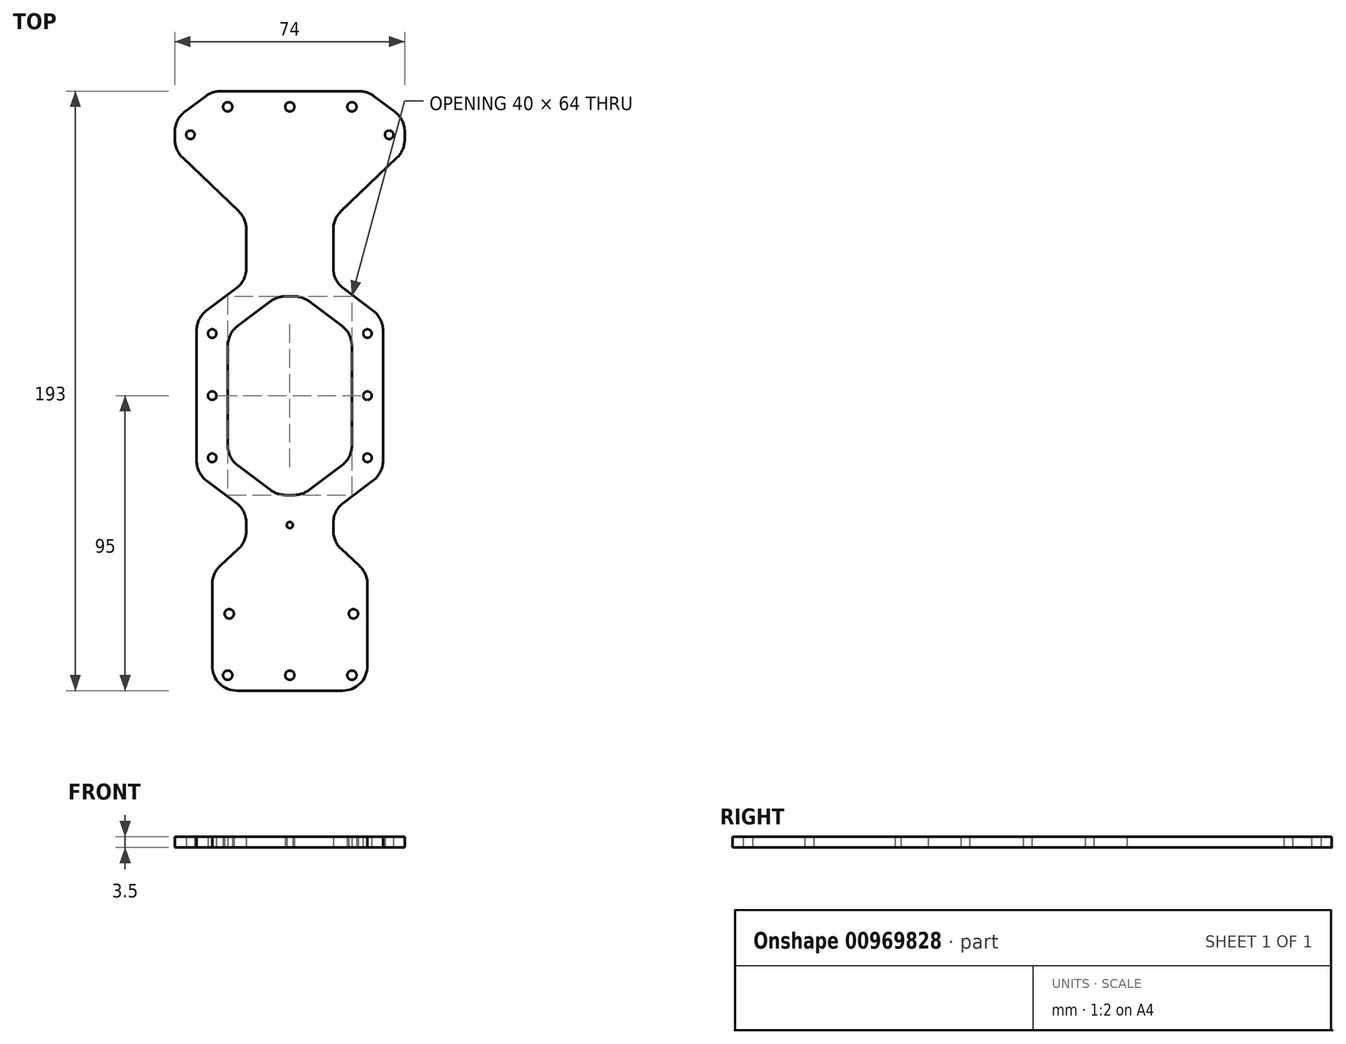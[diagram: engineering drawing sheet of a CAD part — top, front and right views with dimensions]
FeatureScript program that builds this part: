
annotation { "Feature Type Name" : "Feature", "Feature Type Description" : "" }
export const myFeature = defineFeature(function(context is Context, id is Id, definition is map)
    precondition{}
    {
        {
            var Q0;
            Q0=qCreatedBy(makeId("Top.planeOp"),FACE);
            var sketch = newSketch(context, id + "F0", { "sketchPlane" : qUnion([Q0])});
            skCircle(sketch, "E0", {"center": v(-32, 86) * mm, "radius": 1.38 * mm});
            skCircle(sketch, "E1", {"center": v(0, 95) * mm, "radius": 1.5 * mm});
            skCircle(sketch, "E2", {"center": v(-20, 95) * mm, "radius": 1.5 * mm});
            skCircle(sketch, "E3", {"center": v(32, 86) * mm, "radius": 1.38 * mm});
            skCircle(sketch, "E4", {"center": v(20, 95) * mm, "radius": 1.5 * mm});
            skLineSegment(sketch, "E5", {"start": v(0, 95) * mm, "end": v(-20, 95) * mm, "construction": true});
            skLineSegment(sketch, "E6", {"start": v(0, 95) * mm, "end": v(20, 95) * mm, "construction": true});
            skCircle(sketch, "E7", {"center": v(0, -88) * mm, "radius": 1.5 * mm});
            skCircle(sketch, "E8", {"center": v(-20, -88) * mm, "radius": 1.5 * mm});
            skCircle(sketch, "E9", {"center": v(20, -88) * mm, "radius": 1.5 * mm});
            skLineSegment(sketch, "E10", {"start": v(0, -88) * mm, "end": v(-20, -88) * mm, "construction": true});
            skLineSegment(sketch, "E11", {"start": v(0, -88) * mm, "end": v(20, -88) * mm, "construction": true});
            skCircle(sketch, "E12", {"center": v(-25, 22) * mm, "radius": 1.38 * mm});
            skCircle(sketch, "E13", {"center": v(-25, 2) * mm, "radius": 1.38 * mm});
            skCircle(sketch, "E14", {"center": v(-25, -18) * mm, "radius": 1.38 * mm});
            skCircle(sketch, "E15", {"center": v(25, 22) * mm, "radius": 1.38 * mm});
            skCircle(sketch, "E16", {"center": v(25, 2) * mm, "radius": 1.38 * mm});
            skCircle(sketch, "E17", {"center": v(25, -18) * mm, "radius": 1.38 * mm});
            skCircle(sketch, "E18", {"center": v(-19.5, -68.25) * mm, "radius": 1.5 * mm});
            skCircle(sketch, "E19", {"center": v(20.5, -68.25) * mm, "radius": 1.5 * mm});
            skLineSegment(sketch, "E20", {"start": v(-37, 81) * mm, "end": v(-14, 59) * mm});
            skLineSegment(sketch, "E21", {"start": v(-37, 81) * mm, "end": v(-37, 91) * mm});
            skLineSegment(sketch, "E22", {"start": v(-37, 91) * mm, "end": v(-25, 100) * mm});
            skLineSegment(sketch, "E23", {"start": v(-25, 100) * mm, "end": v(25, 100) * mm});
            skPoint(sketch, "E24", {"position": v(-37, 86) * mm});
            skLineSegment(sketch, "E25.MirrorCS", {"start": v(37, 81) * mm, "end": v(37, 91) * mm});
            skLineSegment(sketch, "E26.MirrorCS", {"start": v(37, 91) * mm, "end": v(25, 100) * mm});
            skLineSegment(sketch, "E27.MirrorCS", {"start": v(37, 81) * mm, "end": v(14, 59) * mm});
            skLineSegment(sketch, "E28", {"start": v(-14, 59) * mm, "end": v(-14, 39) * mm});
            skLineSegment(sketch, "E29.MirrorCS", {"start": v(14, 59) * mm, "end": v(14, 39) * mm});
            skLineSegment(sketch, "E30", {"start": v(-14, -45) * mm, "end": v(-25, -55.2) * mm});
            skLineSegment(sketch, "E31", {"start": v(-25, -55.2) * mm, "end": v(-25, -93) * mm});
            skLineSegment(sketch, "E32", {"start": v(-25, -93) * mm, "end": v(25, -93) * mm});
            skLineSegment(sketch, "E33", {"start": v(25, -93) * mm, "end": v(25, -55.2) * mm});
            skLineSegment(sketch, "E34", {"start": v(25, -55.2) * mm, "end": v(14, -45) * mm});
            skLineSegment(sketch, "E35", {"start": v(-14, 39) * mm, "end": v(-30, 27) * mm});
            skLineSegment(sketch, "E36", {"start": v(-30, 27) * mm, "end": v(-30, -23) * mm});
            skLineSegment(sketch, "E37", {"start": v(-30, -23) * mm, "end": v(-14, -35) * mm});
            skPoint(sketch, "E38", {"position": v(-30, 2) * mm});
            skLineSegment(sketch, "E39", {"start": v(-25, 2) * mm, "end": v(-25, 22) * mm, "construction": true});
            skLineSegment(sketch, "E40", {"start": v(-25, 2) * mm, "end": v(-25, -18) * mm, "construction": true});
            skLineSegment(sketch, "E41.MirrorCS", {"start": v(14, 39) * mm, "end": v(30, 27) * mm});
            skLineSegment(sketch, "E42.MirrorCS", {"start": v(30, 27) * mm, "end": v(30, -23) * mm});
            skLineSegment(sketch, "E43.MirrorCS", {"start": v(30, -23) * mm, "end": v(14, -35) * mm});
            skLineSegment(sketch, "E44.trimOffspring", {"start": v(-14, -35) * mm, "end": v(-14, -45) * mm});
            skLineSegment(sketch, "E45.trimOffspring", {"start": v(14, -35) * mm, "end": v(14, -45) * mm});
            skLineSegment(sketch, "E46.0", {"start": v(27, 85.27) * mm, "end": v(27, 86) * mm});
            skLineSegment(sketch, "E46.1", {"start": v(27, 86) * mm, "end": v(21.67, 90) * mm});
            skLineSegment(sketch, "E46.2", {"start": v(-21.67, 90) * mm, "end": v(21.67, 90) * mm});
            skLineSegment(sketch, "E46.3", {"start": v(-27, 86) * mm, "end": v(-21.67, 90) * mm});
            skLineSegment(sketch, "E46.4", {"start": v(-27, 85.27) * mm, "end": v(-27, 86) * mm});
            skLineSegment(sketch, "E46.5", {"start": v(27, 85.27) * mm, "end": v(4, 63.27) * mm});
            skLineSegment(sketch, "E46.6", {"start": v(-27, 85.27) * mm, "end": v(-4, 63.27) * mm});
            skLineSegment(sketch, "E46.7", {"start": v(-4, 63.27) * mm, "end": v(-4, 34) * mm});
            skLineSegment(sketch, "E46.8", {"start": v(-4, 34) * mm, "end": v(-20, 22) * mm});
            skLineSegment(sketch, "E46.9", {"start": v(-20, 22) * mm, "end": v(-20, -18) * mm});
            skLineSegment(sketch, "E46.10", {"start": v(-20, -18) * mm, "end": v(-4, -30) * mm});
            skLineSegment(sketch, "E46.11", {"start": v(-4, -30) * mm, "end": v(-4, -49.37) * mm});
            skLineSegment(sketch, "E46.12", {"start": v(20, -18) * mm, "end": v(4, -30) * mm});
            skLineSegment(sketch, "E46.13", {"start": v(20, 22) * mm, "end": v(20, -18) * mm});
            skLineSegment(sketch, "E46.14", {"start": v(4, 34) * mm, "end": v(20, 22) * mm});
            skLineSegment(sketch, "E46.15", {"start": v(4, 63.27) * mm, "end": v(4, 34) * mm});
            skLineSegment(sketch, "E46.16", {"start": v(4, -30) * mm, "end": v(4, -49.37) * mm});
            skLineSegment(sketch, "E46.17", {"start": v(15, -59.56) * mm, "end": v(4, -49.37) * mm});
            skLineSegment(sketch, "E46.18", {"start": v(15, -83) * mm, "end": v(15, -59.56) * mm});
            skLineSegment(sketch, "E46.19", {"start": v(-15, -83) * mm, "end": v(15, -83) * mm});
            skLineSegment(sketch, "E46.20", {"start": v(-15, -59.56) * mm, "end": v(-15, -83) * mm});
            skLineSegment(sketch, "E46.21", {"start": v(-4, -49.37) * mm, "end": v(-15, -59.56) * mm});
            skCircle(sketch, "E47", {"center": v(0, -39.68) * mm, "radius": 1 * mm});
            skPoint(sketch, "E47.centerSnap0", {"position": v(-4, -39.68) * mm});
            skLineSegment(sketch, "E48", {"start": v(-4, -30) * mm, "end": v(4, -30) * mm});
            skLineSegment(sketch, "E49", {"start": v(-4, 34) * mm, "end": v(4, 34) * mm});
            skSolve(sketch);
        }
        {
            var Q0;
            Q0=makeQuery(id+"F0.imprint","IMPRINT",FACE,{"disambiguationData":[TD([[makeQuery(id+"F0.imprint","IMPRINT",EDGE,{"derivedFrom":sQuery(id+"F0.wireOp",EDGE,"E0")}),-1.0]])]});
            var Q1;
            Q1=makeQuery(id+"F0.imprint","IMPRINT",FACE,{"disambiguationData":[TD([[makeQuery(id+"F0.imprint","IMPRINT",EDGE,{"derivedFrom":sQuery(id+"F0.wireOp",EDGE,"E7")}),-1.0]])]});
            var Q2;
            Q2=makeQuery(id+"F0.imprint","IMPRINT",FACE,{"disambiguationData":[TD([[makeQuery(id+"F0.imprint","IMPRINT",EDGE,{"derivedFrom":sQuery(id+"F0.wireOp",EDGE,"E12")}),-1.0]])]});
            var Q3;
            Q3=makeQuery(id+"F0.imprint","IMPRINT",FACE,{"disambiguationData":[TD([[makeQuery(id+"F0.imprint","IMPRINT",EDGE,{"derivedFrom":sQuery(id+"F0.wireOp",EDGE,"E15")}),-1.0]])]});
            var Q4;
            {var subQ3=sQuery(id+"F0.wireOp",EDGE,"E28");var subQ9=makeQuery(id+"F0.imprint","INTERSECT",VERTEX,{"derivedFrom":[subQ3,sQuery(id+"F0.wireOp",EDGE,"E37")]});Q4=makeQuery(id+"F0.imprint","IMPRINT",FACE,{"disambiguationData":[TD([[makeQuery(id+"F0.imprint","IMPRINT",EDGE,{"disambiguationData":[TD([[subQ9,1.0]])],"derivedFrom":subQ3}),1.0]])]});}
            var Q5;
            {var subQ3=sQuery(id+"F0.wireOp",EDGE,"E29.MirrorCS");var subQ9=makeQuery(id+"F0.imprint","INTERSECT",VERTEX,{"derivedFrom":[subQ3,sQuery(id+"F0.wireOp",EDGE,"E43.MirrorCS")]});Q5=makeQuery(id+"F0.imprint","IMPRINT",FACE,{"disambiguationData":[TD([[makeQuery(id+"F0.imprint","IMPRINT",EDGE,{"disambiguationData":[TD([[subQ9,1.0]])],"derivedFrom":subQ3}),-1.0]])]});}
            var Q6;
            {var subQ3=sQuery(id+"F0.wireOp",EDGE,"E29.MirrorCS");var subQ7=makeQuery(id+"F0.imprint","INTERSECT",VERTEX,{"derivedFrom":[subQ3,sQuery(id+"F0.wireOp",EDGE,"E41.MirrorCS")]});Q6=makeQuery(id+"F0.imprint","IMPRINT",FACE,{"disambiguationData":[TD([[makeQuery(id+"F0.imprint","IMPRINT",EDGE,{"disambiguationData":[TD([[subQ7,-1.0]])],"derivedFrom":subQ3}),-1.0]])]});}
            var Q7;
            {var subQ3=sQuery(id+"F0.wireOp",EDGE,"E28");var subQ9=makeQuery(id+"F0.imprint","INTERSECT",VERTEX,{"derivedFrom":[subQ3,sQuery(id+"F0.wireOp",EDGE,"E35")]});Q7=makeQuery(id+"F0.imprint","IMPRINT",FACE,{"disambiguationData":[TD([[makeQuery(id+"F0.imprint","IMPRINT",EDGE,{"disambiguationData":[TD([[subQ9,-1.0]])],"derivedFrom":subQ3}),1.0]])]});}
            var Q8;
            Q8=makeQuery(id+"F0.imprint","IMPRINT",FACE,{"disambiguationData":[TD([[makeQuery(id+"F0.imprint","IMPRINT",EDGE,{"derivedFrom":sQuery(id+"F0.wireOp",EDGE,"E46.0")}),1.0]])]});
            var Q9;
            Q9=makeQuery(id+"F0.imprint","IMPRINT",FACE,{"disambiguationData":[TD([[makeQuery(id+"F0.imprint","IMPRINT",EDGE,{"derivedFrom":sQuery(id+"F0.wireOp",EDGE,"E46.11")}),1.0]])]});
            extrude(context, id + "F1", {"entities" : qUnion([Q0, Q1, Q2, Q3, Q4, Q5, Q6, Q7, Q8, Q9]), "depth" : 3.5 * mm, "offsetDistance" : 25 * mm});
        }
        {
            var Q0;
            Q0=makeQuery(id+"F1.opExtrude","SWEPT_EDGE",EDGE,{"disambiguationData":[OSD([sQuery(id+"F0.wireOp",EDGE,"E46.19"),sQuery(id+"F0.wireOp",EDGE,"E46.20")])]});
            var Q1;
            Q1=makeQuery(id+"F1.opExtrude","SWEPT_EDGE",EDGE,{"disambiguationData":[OSD([sQuery(id+"F0.wireOp",EDGE,"E46.20"),sQuery(id+"F0.wireOp",EDGE,"E46.21")])]});
            var Q2;
            Q2=makeQuery(id+"F1.opExtrude","SWEPT_EDGE",EDGE,{"disambiguationData":[OSD([sQuery(id+"F0.wireOp",EDGE,"E46.17"),sQuery(id+"F0.wireOp",EDGE,"E46.18")])]});
            var Q3;
            Q3=makeQuery(id+"F1.opExtrude","SWEPT_EDGE",EDGE,{"disambiguationData":[OSD([sQuery(id+"F0.wireOp",EDGE,"E46.16"),sQuery(id+"F0.wireOp",EDGE,"E46.17")])]});
            var Q4;
            Q4=makeQuery(id+"F1.opExtrude","SWEPT_EDGE",EDGE,{"disambiguationData":[OSD([sQuery(id+"F0.wireOp",EDGE,"E46.11"),sQuery(id+"F0.wireOp",EDGE,"E46.21")])]});
            var Q5;
            Q5=makeQuery(id+"F1.opExtrude","SWEPT_EDGE",EDGE,{"disambiguationData":[OSD([sQuery(id+"F0.wireOp",EDGE,"E46.10"),sQuery(id+"F0.wireOp",EDGE,"E46.11")])]});
            var Q6;
            Q6=makeQuery(id+"F1.opExtrude","SWEPT_EDGE",EDGE,{"disambiguationData":[OSD([sQuery(id+"F0.wireOp",EDGE,"E46.12"),sQuery(id+"F0.wireOp",EDGE,"E46.16")])]});
            var Q7;
            Q7=makeQuery(id+"F1.opExtrude","SWEPT_EDGE",EDGE,{"disambiguationData":[OSD([sQuery(id+"F0.wireOp",EDGE,"E46.12"),sQuery(id+"F0.wireOp",EDGE,"E46.13")])]});
            var Q8;
            Q8=makeQuery(id+"F1.opExtrude","SWEPT_EDGE",EDGE,{"disambiguationData":[OSD([sQuery(id+"F0.wireOp",EDGE,"E46.18"),sQuery(id+"F0.wireOp",EDGE,"E46.19")])]});
            var Q9;
            Q9=makeQuery(id+"F1.opExtrude","SWEPT_EDGE",EDGE,{"disambiguationData":[OSD([sQuery(id+"F0.wireOp",EDGE,"E31"),sQuery(id+"F0.wireOp",EDGE,"E32")])]});
            var Q10;
            Q10=makeQuery(id+"F1.opExtrude","SWEPT_EDGE",EDGE,{"disambiguationData":[OSD([sQuery(id+"F0.wireOp",EDGE,"E32"),sQuery(id+"F0.wireOp",EDGE,"E33")])]});
            var Q11;
            Q11=makeQuery(id+"F1.opExtrude","SWEPT_EDGE",EDGE,{"disambiguationData":[OSD([sQuery(id+"F0.wireOp",EDGE,"E33"),sQuery(id+"F0.wireOp",EDGE,"E34")])]});
            var Q12;
            Q12=makeQuery(id+"F1.opExtrude","SWEPT_EDGE",EDGE,{"disambiguationData":[OSD([sQuery(id+"F0.wireOp",EDGE,"E34"),sQuery(id+"F0.wireOp",EDGE,"E45.trimOffspring")])]});
            var Q13;
            Q13=makeQuery(id+"F1.opExtrude","SWEPT_EDGE",EDGE,{"disambiguationData":[OSD([sQuery(id+"F0.wireOp",EDGE,"E30"),sQuery(id+"F0.wireOp",EDGE,"E31")])]});
            var Q14;
            Q14=makeQuery(id+"F1.opExtrude","SWEPT_EDGE",EDGE,{"disambiguationData":[OSD([sQuery(id+"F0.wireOp",EDGE,"E30"),sQuery(id+"F0.wireOp",EDGE,"E44.trimOffspring")])]});
            var Q15;
            Q15=makeQuery(id+"F1.opExtrude","SWEPT_EDGE",EDGE,{"disambiguationData":[OSD([sQuery(id+"F0.wireOp",EDGE,"E37"),sQuery(id+"F0.wireOp",EDGE,"E44.trimOffspring")])]});
            var Q16;
            Q16=makeQuery(id+"F1.opExtrude","SWEPT_EDGE",EDGE,{"disambiguationData":[OSD([sQuery(id+"F0.wireOp",EDGE,"E43.MirrorCS"),sQuery(id+"F0.wireOp",EDGE,"E45.trimOffspring")])]});
            var Q17;
            Q17=makeQuery(id+"F1.opExtrude","SWEPT_EDGE",EDGE,{"disambiguationData":[OSD([sQuery(id+"F0.wireOp",EDGE,"E42.MirrorCS"),sQuery(id+"F0.wireOp",EDGE,"E43.MirrorCS")])]});
            var Q18;
            Q18=makeQuery(id+"F1.opExtrude","SWEPT_EDGE",EDGE,{"disambiguationData":[OSD([sQuery(id+"F0.wireOp",EDGE,"E36"),sQuery(id+"F0.wireOp",EDGE,"E37")])]});
            var Q19;
            Q19=makeQuery(id+"F1.opExtrude","SWEPT_EDGE",EDGE,{"disambiguationData":[OSD([sQuery(id+"F0.wireOp",EDGE,"E46.9"),sQuery(id+"F0.wireOp",EDGE,"E46.10")])]});
            var Q20;
            Q20=makeQuery(id+"F1.opExtrude","SWEPT_EDGE",EDGE,{"disambiguationData":[OSD([sQuery(id+"F0.wireOp",EDGE,"E46.8"),sQuery(id+"F0.wireOp",EDGE,"E46.9")])]});
            var Q21;
            Q21=makeQuery(id+"F1.opExtrude","SWEPT_EDGE",EDGE,{"disambiguationData":[OSD([sQuery(id+"F0.wireOp",EDGE,"E46.13"),sQuery(id+"F0.wireOp",EDGE,"E46.14")])]});
            var Q22;
            Q22=makeQuery(id+"F1.opExtrude","SWEPT_EDGE",EDGE,{"disambiguationData":[OSD([sQuery(id+"F0.wireOp",EDGE,"E46.14"),sQuery(id+"F0.wireOp",EDGE,"E46.15")])]});
            var Q23;
            Q23=makeQuery(id+"F1.opExtrude","SWEPT_EDGE",EDGE,{"disambiguationData":[OSD([sQuery(id+"F0.wireOp",EDGE,"E46.7"),sQuery(id+"F0.wireOp",EDGE,"E46.8")])]});
            var Q24;
            Q24=makeQuery(id+"F1.opExtrude","SWEPT_EDGE",EDGE,{"disambiguationData":[OSD([sQuery(id+"F0.wireOp",EDGE,"E35"),sQuery(id+"F0.wireOp",EDGE,"E36")])]});
            var Q25;
            Q25=makeQuery(id+"F1.opExtrude","SWEPT_EDGE",EDGE,{"disambiguationData":[OSD([sQuery(id+"F0.wireOp",EDGE,"E28"),sQuery(id+"F0.wireOp",EDGE,"E35")])]});
            var Q26;
            Q26=makeQuery(id+"F1.opExtrude","SWEPT_EDGE",EDGE,{"disambiguationData":[OSD([sQuery(id+"F0.wireOp",EDGE,"E41.MirrorCS"),sQuery(id+"F0.wireOp",EDGE,"E42.MirrorCS")])]});
            var Q27;
            Q27=makeQuery(id+"F1.opExtrude","SWEPT_EDGE",EDGE,{"disambiguationData":[OSD([sQuery(id+"F0.wireOp",EDGE,"E29.MirrorCS"),sQuery(id+"F0.wireOp",EDGE,"E41.MirrorCS")])]});
            var Q28;
            Q28=makeQuery(id+"F1.opExtrude","SWEPT_EDGE",EDGE,{"disambiguationData":[OSD([sQuery(id+"F0.wireOp",EDGE,"E46.5"),sQuery(id+"F0.wireOp",EDGE,"E46.15")])]});
            var Q29;
            Q29=makeQuery(id+"F1.opExtrude","SWEPT_EDGE",EDGE,{"disambiguationData":[OSD([sQuery(id+"F0.wireOp",EDGE,"E46.6"),sQuery(id+"F0.wireOp",EDGE,"E46.7")])]});
            var Q30;
            Q30=makeQuery(id+"F1.opExtrude","SWEPT_EDGE",EDGE,{"disambiguationData":[OSD([sQuery(id+"F0.wireOp",EDGE,"E46.4"),sQuery(id+"F0.wireOp",EDGE,"E46.6")])]});
            var Q31;
            Q31=makeQuery(id+"F1.opExtrude","SWEPT_EDGE",EDGE,{"disambiguationData":[OSD([sQuery(id+"F0.wireOp",EDGE,"E46.3"),sQuery(id+"F0.wireOp",EDGE,"E46.4")])]});
            var Q32;
            Q32=makeQuery(id+"F1.opExtrude","SWEPT_EDGE",EDGE,{"disambiguationData":[OSD([sQuery(id+"F0.wireOp",EDGE,"E46.0"),sQuery(id+"F0.wireOp",EDGE,"E46.5")])]});
            var Q33;
            Q33=makeQuery(id+"F1.opExtrude","SWEPT_EDGE",EDGE,{"disambiguationData":[OSD([sQuery(id+"F0.wireOp",EDGE,"E46.0"),sQuery(id+"F0.wireOp",EDGE,"E46.1")])]});
            var Q34;
            Q34=makeQuery(id+"F1.opExtrude","SWEPT_EDGE",EDGE,{"disambiguationData":[OSD([sQuery(id+"F0.wireOp",EDGE,"E46.1"),sQuery(id+"F0.wireOp",EDGE,"E46.2")])]});
            var Q35;
            Q35=makeQuery(id+"F1.opExtrude","SWEPT_EDGE",EDGE,{"disambiguationData":[OSD([sQuery(id+"F0.wireOp",EDGE,"E46.2"),sQuery(id+"F0.wireOp",EDGE,"E46.3")])]});
            var Q36;
            Q36=makeQuery(id+"F1.opExtrude","SWEPT_EDGE",EDGE,{"disambiguationData":[OSD([sQuery(id+"F0.wireOp",EDGE,"E20"),sQuery(id+"F0.wireOp",EDGE,"E28")])]});
            var Q37;
            Q37=makeQuery(id+"F1.opExtrude","SWEPT_EDGE",EDGE,{"disambiguationData":[OSD([sQuery(id+"F0.wireOp",EDGE,"E27.MirrorCS"),sQuery(id+"F0.wireOp",EDGE,"E29.MirrorCS")])]});
            var Q38;
            Q38=makeQuery(id+"F1.opExtrude","SWEPT_EDGE",EDGE,{"disambiguationData":[OSD([sQuery(id+"F0.wireOp",EDGE,"E25.MirrorCS"),sQuery(id+"F0.wireOp",EDGE,"E27.MirrorCS")])]});
            var Q39;
            Q39=makeQuery(id+"F1.opExtrude","SWEPT_EDGE",EDGE,{"disambiguationData":[OSD([sQuery(id+"F0.wireOp",EDGE,"E25.MirrorCS"),sQuery(id+"F0.wireOp",EDGE,"E26.MirrorCS")])]});
            var Q40;
            Q40=makeQuery(id+"F1.opExtrude","SWEPT_EDGE",EDGE,{"disambiguationData":[OSD([sQuery(id+"F0.wireOp",EDGE,"E23"),sQuery(id+"F0.wireOp",EDGE,"E26.MirrorCS")])]});
            var Q41;
            Q41=makeQuery(id+"F1.opExtrude","SWEPT_EDGE",EDGE,{"disambiguationData":[OSD([sQuery(id+"F0.wireOp",EDGE,"E22"),sQuery(id+"F0.wireOp",EDGE,"E23")])]});
            var Q42;
            Q42=makeQuery(id+"F1.opExtrude","SWEPT_EDGE",EDGE,{"disambiguationData":[OSD([sQuery(id+"F0.wireOp",EDGE,"E20"),sQuery(id+"F0.wireOp",EDGE,"E21")])]});
            var Q43;
            Q43=makeQuery(id+"F1.opExtrude","SWEPT_EDGE",EDGE,{"disambiguationData":[OSD([sQuery(id+"F0.wireOp",EDGE,"E21"),sQuery(id+"F0.wireOp",EDGE,"E22")])]});
            fillet(context, id + "F2", {"entities" : qUnion([Q0, Q1, Q2, Q3, Q4, Q5, Q6, Q7, Q8, Q9, Q10, Q11, Q12, Q13, Q14, Q15, Q16, Q17, Q18, Q19, Q20, Q21, Q22, Q23, Q24, Q25, Q26, Q27, Q28, Q29, Q30, Q31, Q32, Q33, Q34, Q35, Q36, Q37, Q38, Q39, Q40, Q41, Q42, Q43]), "radius" : 8 * mm, "tangentPropagation" : true, "allowEdgeOverflow" : false});
        }
    });
